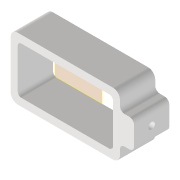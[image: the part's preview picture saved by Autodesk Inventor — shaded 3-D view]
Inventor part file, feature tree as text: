
AUTODESK INVENTOR PART (.ipt)
format: ipt  version: 2022 (Build 260153000, 153)  size: 144,896 bytes
history: native  units: mm
features: extrude x2, sketch x2, other x2, plane x1, fillet x1, reference x1, projected_geometry x1
ambient origin geometry x8: Origin, YZ Plane, XZ Plane, XY Plane, X Axis, Y Axis, Z Axis, Center Point
bodies: Volumenkörper1 (feature_tree)
feature tree (10):
  plane  "Arbeitsebene1"
  extrude  "Extrusion1"  Depth=3.0mm
  fillet  "Rundung1"  Radius=3.0mm
  extrude  "Extrusion2"  Depth=15.0mm TaperAngle=0.0deg
  sketch  "Skizze1"  dims[d0=-15.0mm d1=20.5mm d2=3.0mm]
  reference  "Referenz3"
  sketch  "Skizze2"  dims[d3=3.0mm d4=15.0mm d5=0.0mm d6=6.0mm d7=12.0mm d8=2.0mm d9=2.8mm d10=15.0mm d11=0.0mm]
  projected_geometry  "Projizierte Kontur1"
  other  "Assembly_HoliSheet_v5.iam"
  other  "00_NEMA8:1"
